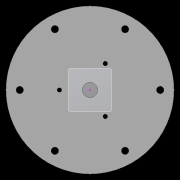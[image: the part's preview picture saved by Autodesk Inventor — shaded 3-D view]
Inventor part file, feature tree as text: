
AUTODESK INVENTOR PART (.ipt)
format: ipt  version: 2022.2 (Build 262287010, 287A)  size: 629,248 bytes
history: native  units: mm
features: extrude x30, sketch x21, other x19, pattern_circular x11, plane x8, fillet x2, move_body x2, revolve x2, draft x2, chamfer x2
ambient origin geometry x8: Origin, YZ Plane, XZ Plane, XY Plane, X Axis, Y Axis, Z Axis, Center Point
bodies: Solid5 (feature_tree)
feature tree (99):
  other  "CrossSection1"
  sketch  "Sketch7"  dims[d167=8.972256mm]
  other  "Roller1"
  other  "Roller2"
  sketch  "Sketch22"  dims[d173=10.814812mm]
  sketch  "Sketch2"  dims[d57=4.025mm d90=61.984365mm]
  sketch  "Sketch23"  dims[d201=75.0mm d232=0.0mm d233=3600.0mm]
  other  "RevRoller1"
  fillet  "Fillet1"  Radius=59.246882mm
  extrude  "Extrusion39"  Depth=61.984365mm
  pattern_circular  "Circular Pattern13"  Count=360  [1 undecoded]
  move_body  "Move Body7"
  revolve  "Revolution13"  [1 undecoded]
  fillet  "Fillet3"  Radius=0.025mm
  pattern_circular  "Circular Pattern14"  Count=24  [1 undecoded]
  move_body  "Move Body6"
  revolve  "Revolution14"  [1 undecoded]
  other  "OuterRim_Top2"
  other  "OuterRim_Bottom2"
  plane  "Work Plane8"
  sketch  "Sketch49"  dims[d352=0.025mm]
  sketch  "Sketch50"  dims[d354=0.025mm]
  sketch  "Sketch51"  dims[d355=16.1595mm]
  extrude  "Extrusion40"  Depth=0.025mm
  extrude  "Extrusion41"  Depth=1.308997mm
  extrude  "Extrusion42"  Depth=5.0mm
  extrude  "Extrusion43"  Depth=5.0mm
  sketch  "Sketch52"  dims[d356=16.159664mm]
  extrude  "Extrusion44"  TaperAngle=360.0deg  [1 undecoded]
  extrude  "Extrusion45"  TaperAngle=90.0deg  [1 undecoded]
  extrude  "Extrusion46"  Depth=5.0mm
  extrude  "Extrusion47"  Depth=5.0mm
  pattern_circular  "Circular Pattern32"  [2 undecoded]
  pattern_circular  "Circular Pattern33"  [2 undecoded]
  sketch  "Sketch57"  dims[d358=360.0deg]
  extrude  "Extrusion50"  Depth=5.0mm
  extrude  "Extrusion51"  Depth=5.0mm
  pattern_circular  "Circular Pattern34"  [2 undecoded]
  extrude  "Extrusion52"  TaperAngle=0.0deg  [1 undecoded]
  extrude  "Extrusion53"  Depth=5.0mm
  pattern_circular  "Circular Pattern35"  [2 undecoded]
  plane  "Work Plane9"
  extrude  "Extrusion54"  Depth=5.0mm
  plane  "Work Plane10"
  sketch  "Sketch60"  dims[d367=8.1mm d370=0.025mm]
  plane  "Work Plane11"
  sketch  "Sketch61"  dims[d371=1.0mm d372=1.308997mm]
  plane  "Work Plane12"
  sketch  "Sketch62"  dims[d373=90.0deg d374=0.5mm d375=240.0mm d376=360.0deg d378=90.0deg d379=0.1mm d380=0.025mm d381=0.025mm d382=0.025mm d383=0.025mm d384=11.193516mm d385=0.0mm d386=0.0mm d391=25.0mm d392=75.0mm d393=1.5mm d394=1.5mm d395=1.5mm d396=1.5mm d397=90.0deg d398=90.0deg d399=90.0deg d400=75.0mm d401=11.193516mm d402=0.0mm d486=0.436332mm d487=0.5mm d488=2.0mm d489=0.0mm d490=20.0mm d495=2.5mm d496=8.0mm d506=13.856406mm d507=55.5mm d508=8.0mm d509=0.05mm d510=2.5mm d511=30.0deg d512=12.0mm d513=6.0mm d514=0.2mm d515=30.0deg d516=131.0mm d517=65.5mm d518=0.2mm d519=100.0mm d520=120.0mm d521=2.0mm d522=150.0mm d530=50.0mm d531=5.5mm d532=5.5mm d533=5.5mm d534=85.75mm d535=73.5mm d536=61.25mm d537=24.5mm d538=3.0mm d539=2.4mm d540=0.0mm d541=0.0mm d542=0.0mm d543=5.5mm d544=3.0mm d545=0.0mm d546=90.0mm d547=360.0deg d549=3.0mm d550=3.0mm d551=2.4mm d552=0.0mm d553=5.596758mm d554=0.0mm d555=2.4mm d556=0.0mm d557=5.596758mm d558=0.0mm d559=5.596758mm d560=0.0mm d561=90.0mm d562=360.0deg d564=60.0mm d565=360.0deg d567=5.5mm d568=5.5mm d569=3.0mm d570=0.0mm d571=5.596758mm d572=0.0mm d573=3.0mm d574=0.0mm d575=5.596758mm d576=0.0mm d577=90.0mm d578=360.0deg d580=60.0mm d581=360.0deg d584=20.0mm d585=8.0mm d587=1.75mm d589=3.0mm d592=2.0mm d593=12.0mm d594=12.0mm d600=0.5mm d601=2.0mm d602=45.0deg d603=0.5mm d604=2.0mm d605=45.0deg d606=0.436332mm d607=0.5mm d608=0.0mm d609=20.0mm d611=360.0deg d613=0.0mm d614=0.0mm d617=0.99971mm d618=100.0mm d620=69.0mm d621=5.0mm d622=0.5mm d623=0.5mm d624=5.0mm d625=0.2mm d626=0.0mm d627=20.0mm d629=69.0mm d630=73.5mm d631=20.0mm d633=6.283185mm d635=5.5mm d636=3.0mm d637=7.0mm d638=4.0mm d639=5.596758mm d640=0.0mm d641=3.0mm d642=0.0mm d643=5.596758mm d644=0.0mm d645=4.0mm d646=0.0mm d647=20.0mm d649=6.283185mm d651=3.0mm d652=4.0mm d653=20.0mm d655=6.283185mm d657=7.0mm d658=5.5mm d659=5.596758mm d660=0.0mm d661=2.593516mm d662=0.0mm d663=5.596758mm d664=0.0mm d665=3.193516mm d666=0.0mm d679=50.0mm d680=360.0deg d682=50.0mm d683=360.0deg d694=6.35mm d695=6.35mm d696=6.9mm d697=5.9mm d698=11.194mm d699=0.0mm d700=8.194mm d701=0.0mm d702=60.0mm d703=360.0deg d705=30.0deg d706=4.0mm d707=7.0mm d708=3.193516mm d709=0.0mm d710=11.193516mm d711=0.0mm d712=60.0mm d713=360.0deg d715=20.0mm d717=60.0deg d718=5.0mm d719=0.0mm d720=1.0mm d721=50.0mm d724=5.0mm d725=0.0mm d16=0.872665mm d17=0.872665mm d49=0.872665mm d50=0.872665mm d51=0.872665mm d52=0.872665mm d236=0.5mm d237=0.872665mm d238=0.5mm d239=0.872665mm d282=1.0mm d283=1.0mm d284=1.0mm d285=0.15mm d286=0.25mm d287=0.375mm d288=14.3117mm d289=0.75mm d290=20.594885mm d291=0.0625mm d292=0.75mm d293=0.375mm d405=0.5mm d406=0.872665mm d407=0.5mm d408=0.872665mm d413=0.5mm d414=0.872665mm d415=0.5mm d416=0.872665mm d417=0.5mm d418=0.872665mm d419=0.5mm d420=0.872665mm d421=0.872665mm d431=0.5mm d432=0.872665mm d433=0.5mm d434=0.872665mm d471=0.5mm d472=0.872665mm d473=0.5mm d474=0.872665mm d497=0.5mm d498=0.872665mm d499=0.5mm d500=0.872665mm d590=0.5mm d591=0.872665mm]
  extrude  "Extrusion56"  Depth=5.0mm
  plane  "Work Plane7"
  sketch  "Sketch47"  dims[d350=47.575427mm]
  extrude  "Rotor_Ring"  Depth=5.0mm
  draft  "FaceDraft2"
  sketch  "Sketch30"  dims[d343=16.1595mm d344=16.159664mm d345=0.025mm]
  plane  "Work Plane5"
  other  "Rotor Featurs"
  other  "RotorRim_Bottom"
  extrude  "Extrusion24"  Depth=5.0mm
  extrude  "Extrusion25"  TaperAngle=90.0deg  [1 undecoded]
  extrude  "Extrusion26"  TaperAngle=90.0deg  [1 undecoded]
  pattern_circular  "Circular Pattern23"  Angle=90.0deg  [1 undecoded]
  sketch  "Sketch41"  dims[d347=0.1mm]
  extrude  "Extrusion27"  Depth=5.0mm
  extrude  "Extrusion28"  Depth=5.0mm
  pattern_circular  "Circular Pattern24"  [2 undecoded]
  extrude  "Extrusion29"  Depth=5.0mm
  extrude  "Extrusion30"  Depth=2.0mm TaperAngle=0.0deg
  extrude  "Extrusion31"  Depth=5.0mm
  pattern_circular  "Circular Pattern25"  [2 undecoded]
  sketch  "Sketch42"  dims[d348=0.1mm]
  extrude  "Extrusion32"  Depth=5.0mm
  extrude  "Extrusion33"  Depth=5.0mm TaperAngle=30.0deg
  extrude  "Extrusion34"  Depth=5.0mm
  extrude  "Extrusion35"  Depth=5.0mm TaperAngle=30.0deg
  pattern_circular  "Circular Pattern26"  [2 undecoded]
  pattern_circular  "Circular Pattern27"  [2 undecoded]
  chamfer  "Chamfer1"  Distance=0.2mm
  chamfer  "Chamfer2"  Distance=100.0mm
  draft  "FaceDraft4"
  plane  "Work Plane6"
  sketch  "Sketch43"  dims[d349=47.575591mm]
  extrude  "Extrusion37"  Depth=2.0mm
  extrude  "Extrusion38"  Depth=5.0mm
  other  "2D Equation Curve1"
  sketch  "Sketch40"  dims[d346=0.025mm]
  other  "Work Axis6"
  other  "Work Axis7"
  other  "Work Axis8"
  other  "Work Axis9"
  other  "Work Axis10"
  other  "Work Point1"
  other  "Work Point2"
  other  "Work Point3"
  other  "Work Point4"
  other  "Work Point5"
  sketch  "Sketch48"  dims[d351=0.025mm]
  sketch  "Sketch58"  dims[d359=0.5mm d360=240.0mm]
  sketch  "Sketch59"  dims[d361=360.0deg d363=1.308997mm]
note: 26 required parameter values undecoded (feature->parameter linkage not recoverable at this tier; creation-order binding heuristic only, values carry confidence <= 0.55)